# Revit family: Painel Repetidor Endereçável PRC ILUMAC
name_source: partatom
category: Dispositivos de alarme de incêndio
units: mm (PartAtom-declared; Revit-internal decimal feet)

## family parameters
Com base no plano de trabalho = Não
Compartilhado = Não
Corte com vazios quando carregada = Não
Cota do conector redondo = Utilizar diâmetro
Manter orientação da anotação = Não
Número OmniClass = 23.75.00.00
Ponto de cálculo do ambiente = Não
Sempre na vertical = Sim
Tipo de parte = Normal
Título OmniClass = Climate Control (HVAC)

## types (3) — shared parameters
Bornes para conexão dos condutores = KRE p/ 1,5mm² à 2,5mm²
Consumo de energia da rede elétrica = 62 Watts
Correntes de consumo = 30mA @ 24VCC em supervisão
115mA @ 24VCC em alarme
Dimensões (AxLxP) = 255x230x100mm
Fabricante = ILUMAC
Grau de proteção = IP20 (uso interno)
MATERIAL = Plastico branco
Material da caixa = Plástico ABS branco
Relógio = o RTC com data e hora
zero-valued in all types: Elevação padrão

## per-type parameters (varying)
| type | Alimentação principal da rede elétrica | Alimentação secundária | Corrente de recarga das baterias | Código do produto | Descrição | Fixação | Impedância do drive de comunicação | Normas técnicas aplicáveis | Painel frontal (IHM) | Peso | Proteção na entrada da rede elétrica | Proteção na entrada das baterias | Protocolo de comunicação | Saída da fonte de alimentação | Saída para sirenes convencionais | Saída rele auxiliar | Secção dos condutores do cabo | Sinalização sonora interna | Temperatura de operação | Tensão nominal e de operação | Topologia | Umidade relativa |
| PRC-E – BRANCO | a 100 a 240VCA – 50/60Hz | 24VCC (2 baterias seladas de 12VCC - 2,2Ah) | 400mA @ 27,6VCC nominal 25ºC | 002215 | Painel Repetidor Endereçável PRC-E branco | Sobrepor, com 3 parafusos (acompanha) |  | ABNT NBR 17.240:2010 / ISO 7240-4 | ) 6 LEDs / 4 teclas / LCD 2x16 com backlight | 1,8Kg (sem baterias)
3,0Kg (com 2 baterias de 12VCC - 2,2Ah) | Fusível de vidro 20AG - 2A (fusão rápida) | Fusível rearmável - PTC 3A @ 24VCC (25ºC) | ALF-500 (Exclusivo da ILUMAC) | 1,0A @ 28VCC - 25ºC | 1 saída de 2A @ 24VCC | 1 saída contato seco / 1A até 30V (carga resistiva) |  |  | 0 a 40ºC | 24VCC / 22 à 28VCC | Classe A ou Classe B (3 fios) | Máximo 95%, sem condensação |
| PRC-E – PRETO | a 100 a 240VCA – 50/60Hz | 24VCC (2 baterias seladas de 12VCC - 2,2Ah) | 400mA @ 27,6VCC nominal 25ºC | 002214 | Painel Repetidor Endereçável PRC-E preto | Sobrepor, com 3 parafusos (acompanha) |  | ABNT NBR 17.240:2010 / ISO 7240-4 | ) 6 LEDs / 4 teclas / LCD 2x16 com backlight | 1,8Kg (sem baterias)
3,0Kg (com 2 baterias de 12VCC - 2,2Ah) | Fusível de vidro 20AG - 2A (fusão rápida) | Fusível rearmável - PTC 3A @ 24VCC (25ºC) | ALF-500 (Exclusivo da ILUMAC) | 1,0A @ 28VCC - 25ºC | 1 saída de 2A @ 24VCC | 1 saída contato seco / 1A até 30V (carga resistiva) |  |  | 0 a 40ºC | 24VCC / 22 à 28VCC | Classe A ou Classe B (3 fios) | Máximo 95%, sem condensação |
| PRC-D | 100 à 240VCA – 60Hz | 24Vcc (2 baterias seladas de 12V 2,2 A/h) | 400mA @ 27,6VCC nominal 25oC |  | Painel Repetidor Endereçável Sirius PRC-D | Sobrepor | 320KΩ | NBR 17240 / ISO 7240-4 | 6 LEDs / 4 teclas / LCD 2x16 com backlight | 1,8Kg (sem baterias)
3,0Kg (com 2 baterias de 12V 2,2A/h)
3,0Kg (com 2 baterias de 12VCC - 2,2Ah) | Fusível de vidro 20AG- 2A (fusão rápida) | Fusível rearmável-PTC 3A @ 24Vcc (25oC) | ALF-1000-2 (proprietário) | 1,0A @ 28Vcc - 25oC. | 1 saída de 2A @ 24Vcc | 1 saída contato seco 1A @ 30V (carga resistiva) | Mínima de 1,5mm2 e máxima de 2,5mm2 | Buzzer 70dB | 0 à 40°C | 24Vcc (22 à 28Vcc) | Classe A ou B (2 fios) | Máximo 85% sem condensação. |

note: column(s) folded — value = type name in every type: Modelo
